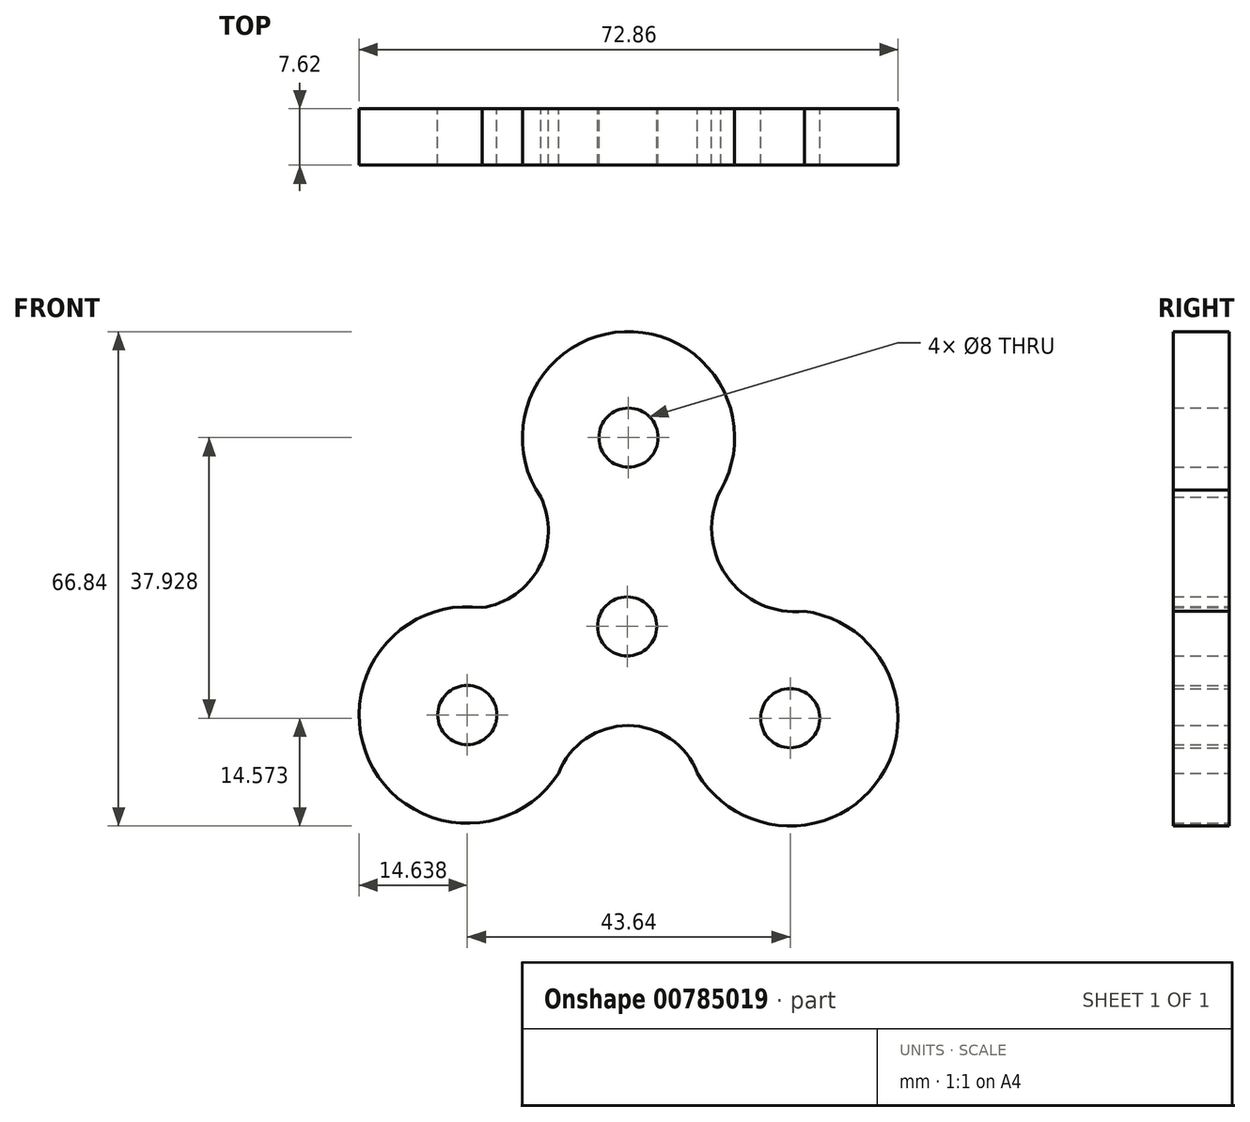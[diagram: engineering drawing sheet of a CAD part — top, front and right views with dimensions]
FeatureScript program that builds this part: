
annotation { "Feature Type Name" : "Feature", "Feature Type Description" : "" }
export const myFeature = defineFeature(function(context is Context, id is Id, definition is map)
    precondition{}
    {
        {
            var Q0;
            Q0=qCreatedBy(makeId("Front.planeOp"),FACE);
            var sketch = newSketch(context, id + "F0", { "sketchPlane" : qUnion([Q0])});
            skArc(sketch, "E0", {"start": v(12.64, 18.41) * mm, "mid": v(-0.39, 39.85) * mm, "end": v(-11.67, 17.45) * mm});
            skArc(sketch, "E1", {"start": v(-19.62, 2.53) * mm, "mid": v(-11.89, 7.99) * mm, "end": v(-11.67, 17.45) * mm});
            skArc(sketch, "E2", {"start": v(-19.62, 2.53) * mm, "mid": v(-34.89, -18.12) * mm, "end": v(-9.27, -19.86) * mm});
            skArc(sketch, "E3", {"start": v(9.5, -19.86) * mm, "mid": v(0.12, -13.41) * mm, "end": v(-9.27, -19.86) * mm});
            skArc(sketch, "E4", {"start": v(9.5, -19.86) * mm, "mid": v(34.2, -20.43) * mm, "end": v(23.95, 2.05) * mm});
            skArc(sketch, "E5", {"start": v(12.64, 18.41) * mm, "mid": v(13.4, 6.85) * mm, "end": v(23.95, 2.05) * mm});
            skCircle(sketch, "E6", {"center": v(0.18, 25.52) * mm, "radius": 4 * mm});
            skCircle(sketch, "E7", {"center": v(-21.6, -11.98) * mm, "radius": 4 * mm});
            skCircle(sketch, "E8", {"center": v(22.04, -12.4) * mm, "radius": 4 * mm});
            skCircle(sketch, "E9", {"center": v(0, 0) * mm, "radius": 4 * mm});
            skSolve(sketch);
        }
        {
            var Q0;
            Q0 = qSketchRegion(id + "F0", true);
            extrude(context, id + "F1", {"entities" : qUnion([Q0]), "depth" : 7.62 * mm, "offsetDistance" : 25.4 * mm});
        }
    });
